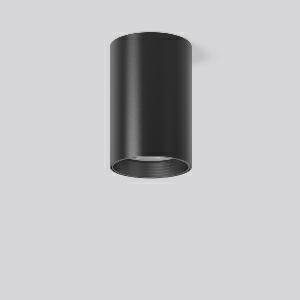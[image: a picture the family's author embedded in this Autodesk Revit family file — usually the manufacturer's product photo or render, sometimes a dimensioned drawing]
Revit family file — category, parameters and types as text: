
# Revit family: heledon_maxi_a_931222_003_4988
name_source: partatom
category: Lighting Fixtures
units: mm (PartAtom-declared; Revit-internal decimal feet)

## family parameters
Cut with Voids When Loaded = No
Host = Face
Light Source = No
Part Type = Normal
Room Calculation Point = No
Round Connector Dimension = Use Diameter
Shared = No

## types (1)
- HELEDON maxi A (1 x LED Modul 930, 2800 lm, 3000)
    Apparent Load = 25 VA
    Approval mark = CE
    CIE Flux Codes = 96 100 100 100 100
    Color Rendering = 90
    Color Temperature = 3000
    Default Elevation = 1800 mm
    Description = Series: HELEDON maxi
Cylindrical surface-mounted downlight. Housing: die-cast aluminium, powder-coated. Internal ceiling frame polycarbonate with bayonet mounting. Black plastic ring and recessed LED to prevent glare from the side. Optical assembly with lens made of plastic (polycarbonate) for the best homogeneous light distribution - can be changed without tools. Best colour rendering index Ra>90. Suitable for Ceiling mounting. Easy installation with a separate ceiling frame with bayonet mounting and plug connection. Driver integrated. Connected via plug-in connector. High quality converter without flickering and stroboscopic effect. The following accessories can be mounted without use of tools: interchangeable lenses, decorative glasses, honeycomb louvre, clear and frosted diffusers, white interchangeable plastic ring. 
Colour: deep black, matt (RAL 9005)
Diameter: 123 mm
Height: 183 mm
Lamp: LED
Socket: without socket
Colour temperature: 3000K
Colour rendering index (CRI): 92
System power: 25 W
Rated luminous flux: 2800 lm
Luminous efficiency: 112 lm/W
Control gear: Regulated power supply
Protection class: I
Type of protection: IP 20
    Height = 183 mm
    Lamp = 1 x LED Modul 930
    Lamp Light Flux = 2800 lm
    Lamp count = 1
    Length = 123 mm
    Lifetime = 50000 h
    Luminous efficacy = 112 lm/W
    Manufacturer = RZB
    ModVariant = No
    Model = 931222.003
    Mounting Place = Ceiling
    Mounting Type = Surface mounted
    Number of Poles = 1
    OnlyDefault = Yes
    Power Factor = 1
    Product Name = HELEDON maxi A
    Product group = Surface mounted downlights
    ProductGroupID = 302
    Protection Class = Protection class I
    Protection Degree = IP 20
    RLX_Detail_Level = 1
    RLX_Emergency_Light_Flux = 0 lm
    RLX_Emergency_Type = 0
    RLX_Emergency_Type_DB = No
    RlxData = <blob elided: 97633 chars, md5=3a7e312e>
    Socket = socket
    Standby Power = 0 W
    System Light Flux = 2800 lm
    System Power = 25 W
    Type Comments = Product without accessories
    Type Image = 931193.003.jpg
    URL = http://relux.com
    VarID = ---
    Voltage = 230 V
    Voltage Range = 220-240 V
    Weight = 0.00 kg
    Width = 0 mm  [stored 0 ft]

note: [stored X ft] marks values corroborated as IEEE doubles in the binary element streams (Revit-internal decimal feet)

## geometry (parser evidence)
native form markers: Blend x4, Sweep x9
no freeform markers — native parametric forms only
